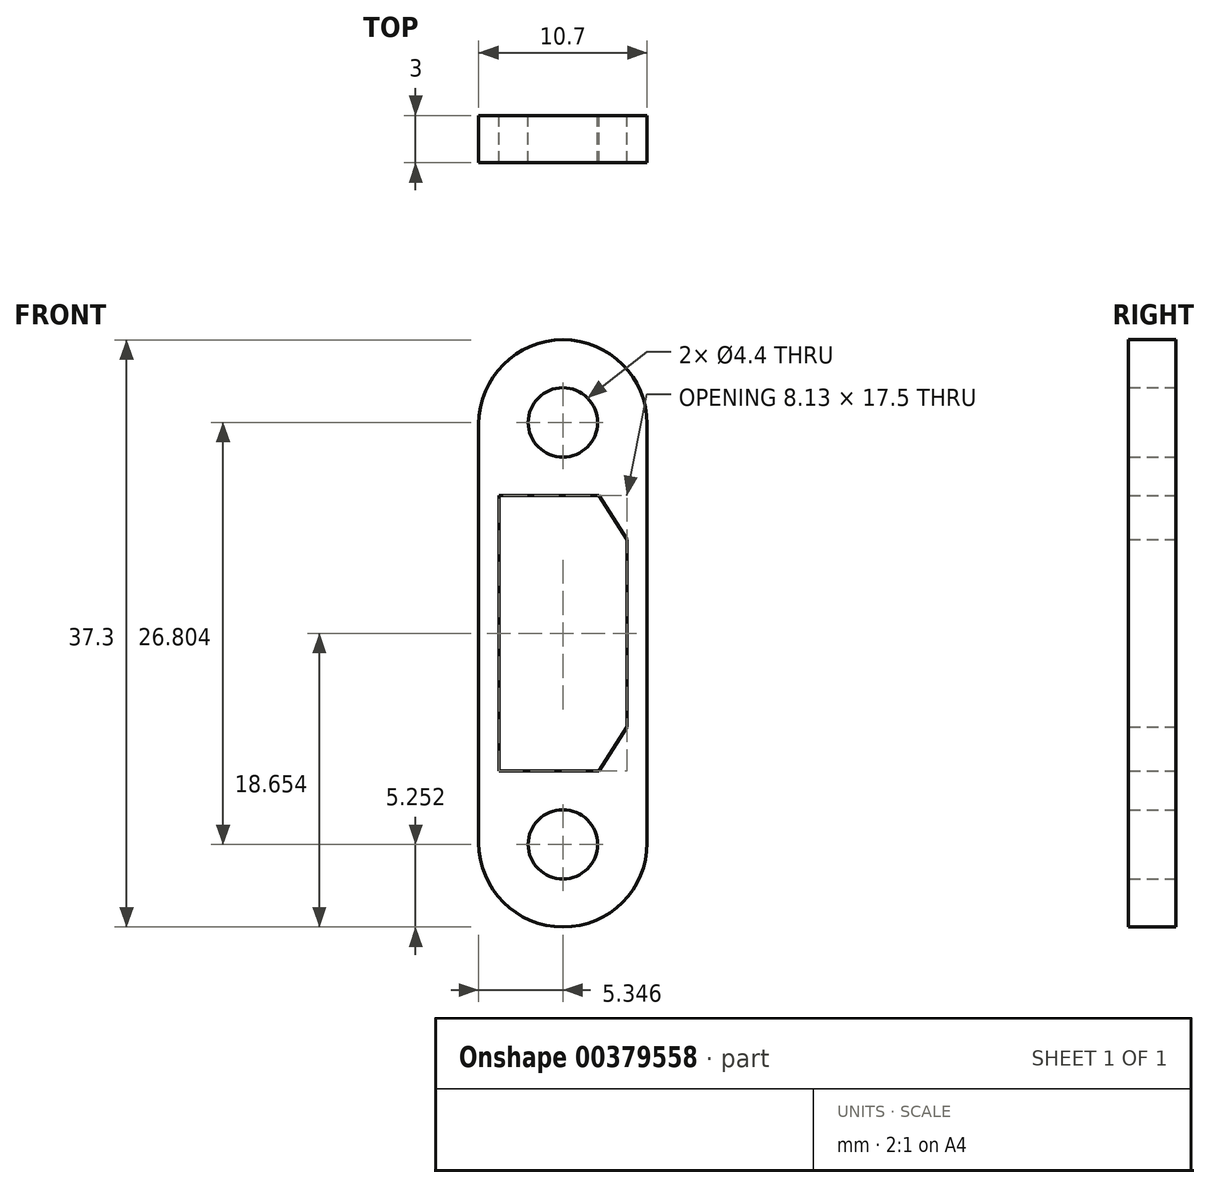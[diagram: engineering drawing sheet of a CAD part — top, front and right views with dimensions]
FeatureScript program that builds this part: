
annotation { "Feature Type Name" : "Feature", "Feature Type Description" : "" }
export const myFeature = defineFeature(function(context is Context, id is Id, definition is map)
    precondition{}
    {
        {
            var Q0;
            Q0=qCreatedBy(makeId("Front.planeOp"),FACE);
            var sketch = newSketch(context, id + "F0", { "sketchPlane" : qUnion([Q0])});
            skLineSegment(sketch, "E0.bottom", {"start": v(-12.53, 40.98) * mm, "end": v(-12.54, 40.98) * mm});
            skLineSegment(sketch, "E0.top", {"start": v(-12.53, 3.68) * mm, "end": v(-12.54, 3.68) * mm});
            skLineSegment(sketch, "E0.left", {"start": v(-7.2, 35.64) * mm, "end": v(-7.2, 9.03) * mm});
            skLineSegment(sketch, "E0.right", {"start": v(-17.9, 35.64) * mm, "end": v(-17.9, 9.03) * mm});
            skArc(sketch, "E1.filletArc", {"start": v(-12.54, 40.98) * mm, "mid": v(-16.32, 39.42) * mm, "end": v(-17.9, 35.64) * mm});
            skArc(sketch, "E2.filletArc", {"start": v(-17.9, 9.03) * mm, "mid": v(-16.32, 5.25) * mm, "end": v(-12.54, 3.68) * mm});
            skArc(sketch, "E3.filletArc", {"start": v(-7.2, 35.64) * mm, "mid": v(-8.75, 39.42) * mm, "end": v(-12.53, 40.98) * mm});
            skArc(sketch, "E4.filletArc", {"start": v(-12.53, 3.68) * mm, "mid": v(-8.75, 5.25) * mm, "end": v(-7.2, 9.03) * mm});
            skLineSegment(sketch, "E5", {"start": v(-12.54, 40.98) * mm, "end": v(-12.53, 40.98) * mm, "construction": true});
            skLineSegment(sketch, "E6", {"start": v(-24.83, 37.94) * mm, "end": v(-1.05, 37.94) * mm, "construction": true});
            skLineSegment(sketch, "E7", {"start": v(-24.83, 35.74) * mm, "end": v(0.63, 35.74) * mm, "construction": true});
            skLineSegment(sketch, "E8", {"start": v(-12.54, 42.28) * mm, "end": v(-12.54, 30.47) * mm, "construction": true});
            skCircle(sketch, "E9", {"center": v(-12.54, 35.74) * mm, "radius": 2.2 * mm});
            skLineSegment(sketch, "E10", {"start": v(-30.87, 22.33) * mm, "end": v(7.43, 22.33) * mm, "construction": true});
            skCircle(sketch, "E11.MirrorC", {"center": v(-12.54, 8.93) * mm, "radius": 2.2 * mm});
            skLineSegment(sketch, "E12.MirrorCS", {"start": v(-24.83, 8.93) * mm, "end": v(0.63, 8.93) * mm, "construction": true});
            skLineSegment(sketch, "E13.MirrorCS", {"start": v(-24.83, 6.73) * mm, "end": v(-1.05, 6.73) * mm, "construction": true});
            skLineSegment(sketch, "E14.MirrorCS", {"start": v(-12.54, 2.38) * mm, "end": v(-12.54, 14.2) * mm, "construction": true});
            skLineSegment(sketch, "E15.bottom", {"start": v(-10.26, 13.58) * mm, "end": v(-16.6, 13.58) * mm});
            skLineSegment(sketch, "E15.top", {"start": v(-10.26, 31.08) * mm, "end": v(-16.6, 31.08) * mm});
            skLineSegment(sketch, "E15.left", {"start": v(-8.48, 16.38) * mm, "end": v(-8.48, 28.29) * mm});
            skLineSegment(sketch, "E15.right", {"start": v(-16.6, 13.58) * mm, "end": v(-16.6, 31.08) * mm});
            skPoint(sketch, "E15.middle", {"position": v(-12.54, 22.33) * mm});
            skLineSegment(sketch, "E16", {"start": v(-10.26, 32.44) * mm, "end": v(-10.26, 12.14) * mm, "construction": true});
            skLineSegment(sketch, "E17", {"start": v(-18.85, 28.29) * mm, "end": v(-4.95, 28.29) * mm, "construction": true});
            skLineSegment(sketch, "E18", {"start": v(-10.26, 31.08) * mm, "end": v(-8.48, 28.29) * mm});
            skLineSegment(sketch, "E19.MirrorCS", {"start": v(-10.26, 13.58) * mm, "end": v(-8.48, 16.38) * mm});
            skSolve(sketch);
        }
        {
            var Q0;
            Q0=makeQuery(id+"F0.imprint","IMPRINT",FACE,{"disambiguationData":[TD([[makeQuery(id+"F0.imprint","IMPRINT",EDGE,{"derivedFrom":sQuery(id+"F0.wireOp",EDGE,"E0.bottom")}),1.0]])]});
            extrude(context, id + "F1", {"entities" : qUnion([Q0]), "depth" : 3 * mm});
        }
    });
